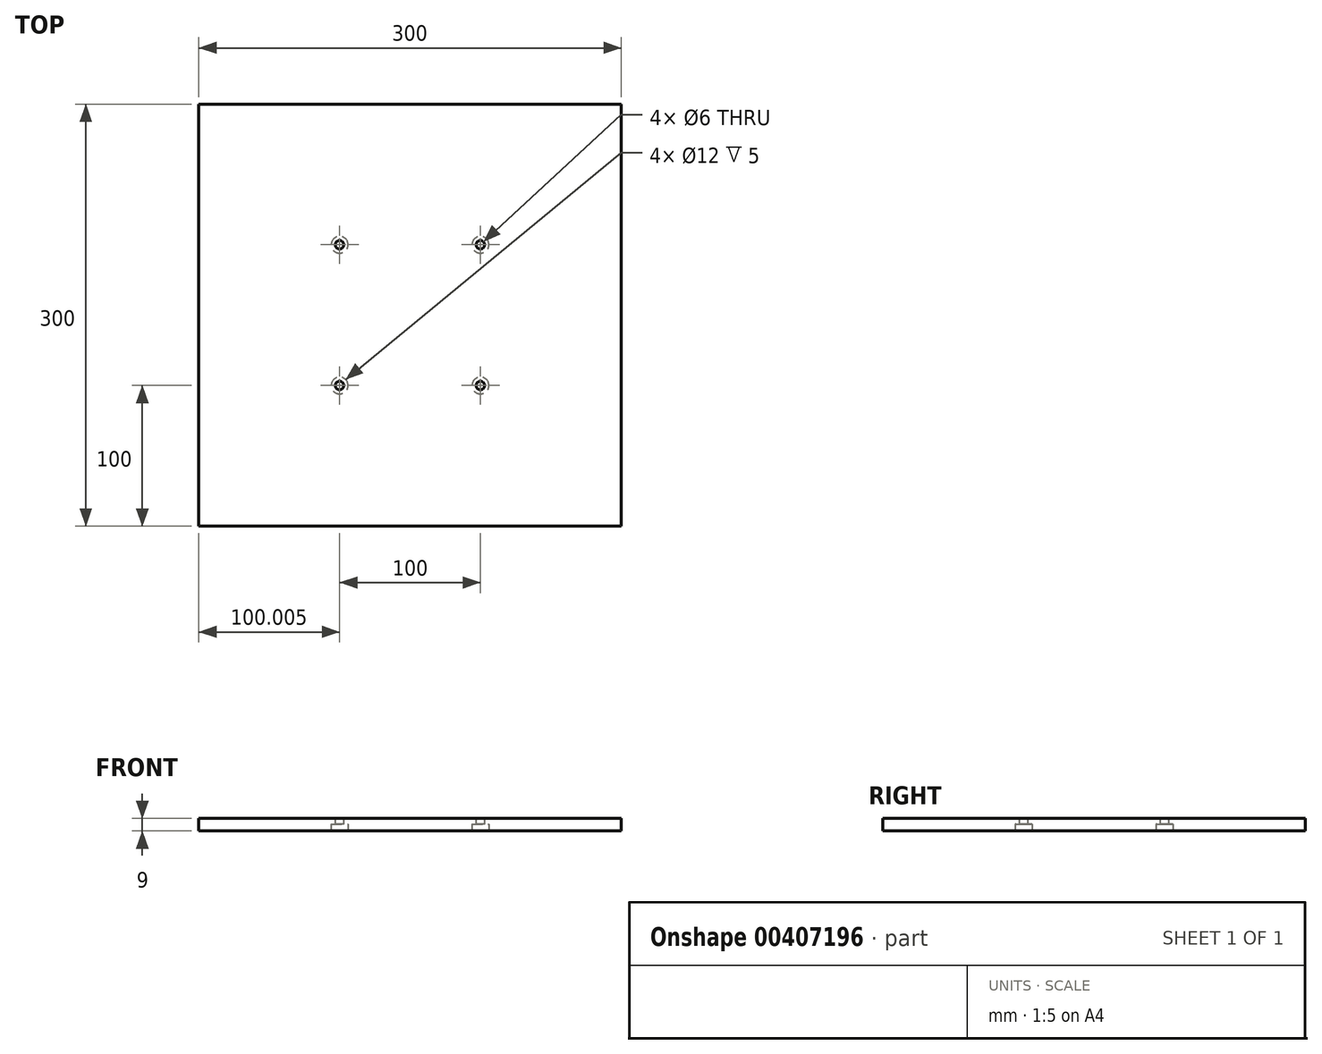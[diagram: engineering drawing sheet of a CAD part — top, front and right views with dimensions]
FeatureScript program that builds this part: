
annotation { "Feature Type Name" : "Feature", "Feature Type Description" : "" }
export const myFeature = defineFeature(function(context is Context, id is Id, definition is map)
    precondition{}
    {
        {
            var Q0;
            Q0=qCreatedBy(makeId("Top.planeOp"),FACE);
            var sketch = newSketch(context, id + "F0", { "sketchPlane" : qUnion([Q0])});
            skLineSegment(sketch, "E0.bottom", {"start": v(-149.07, 122.35) * mm, "end": v(150.93, 122.35) * mm});
            skLineSegment(sketch, "E0.top", {"start": v(-149.07, -177.65) * mm, "end": v(150.93, -177.65) * mm});
            skLineSegment(sketch, "E0.left", {"start": v(-149.07, 122.35) * mm, "end": v(-149.07, -177.65) * mm});
            skLineSegment(sketch, "E0.right", {"start": v(150.93, 122.35) * mm, "end": v(150.93, -177.65) * mm});
            skSolve(sketch);
        }
        {
            var Q0;
            Q0 = qSketchRegion(id + "F0", true);
            extrude(context, id + "F1", {"entities" : qUnion([Q0]), "depth" : 9 * mm});
        }
        {
            var Q0;
            Q0=makeQuery(id+"F1.opExtrude","CAP_FACE",FACE,{"disambiguationData":[OSD([sQuery(id+"F0.wireOp",EDGE,"E0.bottom"),sQuery(id+"F0.wireOp",EDGE,"E0.top"),sQuery(id+"F0.wireOp",EDGE,"E0.left"),sQuery(id+"F0.wireOp",EDGE,"E0.right")])],"isStart":false});
            var sketch = newSketch(context, id + "F2", { "sketchPlane" : qUnion([Q0])});
            skLineSegment(sketch, "E1.bottom", {"start": v(-49.07, 22.35) * mm, "end": v(50.93, 22.35) * mm, "construction": true});
            skLineSegment(sketch, "E1.top", {"start": v(-49.07, -77.65) * mm, "end": v(50.93, -77.65) * mm, "construction": true});
            skLineSegment(sketch, "E1.left", {"start": v(-49.07, 22.35) * mm, "end": v(-49.07, -77.65) * mm, "construction": true});
            skLineSegment(sketch, "E1.right", {"start": v(50.93, 22.35) * mm, "end": v(50.93, -77.65) * mm, "construction": true});
            skCircle(sketch, "E2", {"center": v(-49.07, 22.35) * mm, "radius": 3 * mm});
            skCircle(sketch, "E3", {"center": v(-49.07, -77.65) * mm, "radius": 3 * mm});
            skCircle(sketch, "E4", {"center": v(50.93, -77.65) * mm, "radius": 3 * mm});
            skCircle(sketch, "E5", {"center": v(50.93, 22.35) * mm, "radius": 3 * mm});
            skSolve(sketch);
        }
        {
            var Q0;
            Q0 = qSketchRegion(id + "F2", true);
            extrude(context, id + "F3", {"entities" : qUnion([Q0]), "operationType" : NewBodyOperationType.REMOVE, "endBound" : BoundingType.THROUGH_ALL, "oppositeDirection" : true, "depth" : 25 * mm});
        }
        {
            var Q0;
            Q0=makeQuery(id+"F1.opExtrude","CAP_FACE",FACE,{"disambiguationData":[OSD([sQuery(id+"F0.wireOp",EDGE,"E0.bottom"),sQuery(id+"F0.wireOp",EDGE,"E0.top"),sQuery(id+"F0.wireOp",EDGE,"E0.left"),sQuery(id+"F0.wireOp",EDGE,"E0.right")])],"isStart":true});
            var sketch = newSketch(context, id + "F4", { "sketchPlane" : qUnion([Q0])});
            skCircle(sketch, "E6", {"center": v(-49.07, 77.65) * mm, "radius": 6 * mm});
            skCircle(sketch, "E7", {"center": v(50.93, 77.65) * mm, "radius": 6 * mm});
            skCircle(sketch, "E8", {"center": v(-49.07, -22.35) * mm, "radius": 6 * mm});
            skCircle(sketch, "E9", {"center": v(50.93, -22.35) * mm, "radius": 6 * mm});
            skSolve(sketch);
        }
        {
            var Q0;
            Q0=makeQuery(id+"F4.imprint","IMPRINT",FACE,{"disambiguationData":[TD([[makeQuery(id+"F4.imprint","IMPRINT",EDGE,{"derivedFrom":sQuery(id+"F4.wireOp",EDGE,"E6")}),1.0]])]});
            var Q1;
            Q1=makeQuery(id+"F4.imprint","IMPRINT",FACE,{"disambiguationData":[TD([[makeQuery(id+"F4.imprint","IMPRINT",EDGE,{"derivedFrom":sQuery(id+"F4.wireOp",EDGE,"E7")}),1.0]])]});
            var Q2;
            Q2=makeQuery(id+"F4.imprint","IMPRINT",FACE,{"disambiguationData":[TD([[makeQuery(id+"F4.imprint","IMPRINT",EDGE,{"derivedFrom":sQuery(id+"F4.wireOp",EDGE,"E8")}),1.0]])]});
            var Q3;
            Q3=makeQuery(id+"F4.imprint","IMPRINT",FACE,{"disambiguationData":[TD([[makeQuery(id+"F4.imprint","IMPRINT",EDGE,{"derivedFrom":sQuery(id+"F4.wireOp",EDGE,"E9")}),1.0]])]});
            extrude(context, id + "F5", {"entities" : qUnion([Q0, Q1, Q2, Q3]), "operationType" : NewBodyOperationType.REMOVE, "oppositeDirection" : true, "depth" : 5 * mm});
        }
    });
